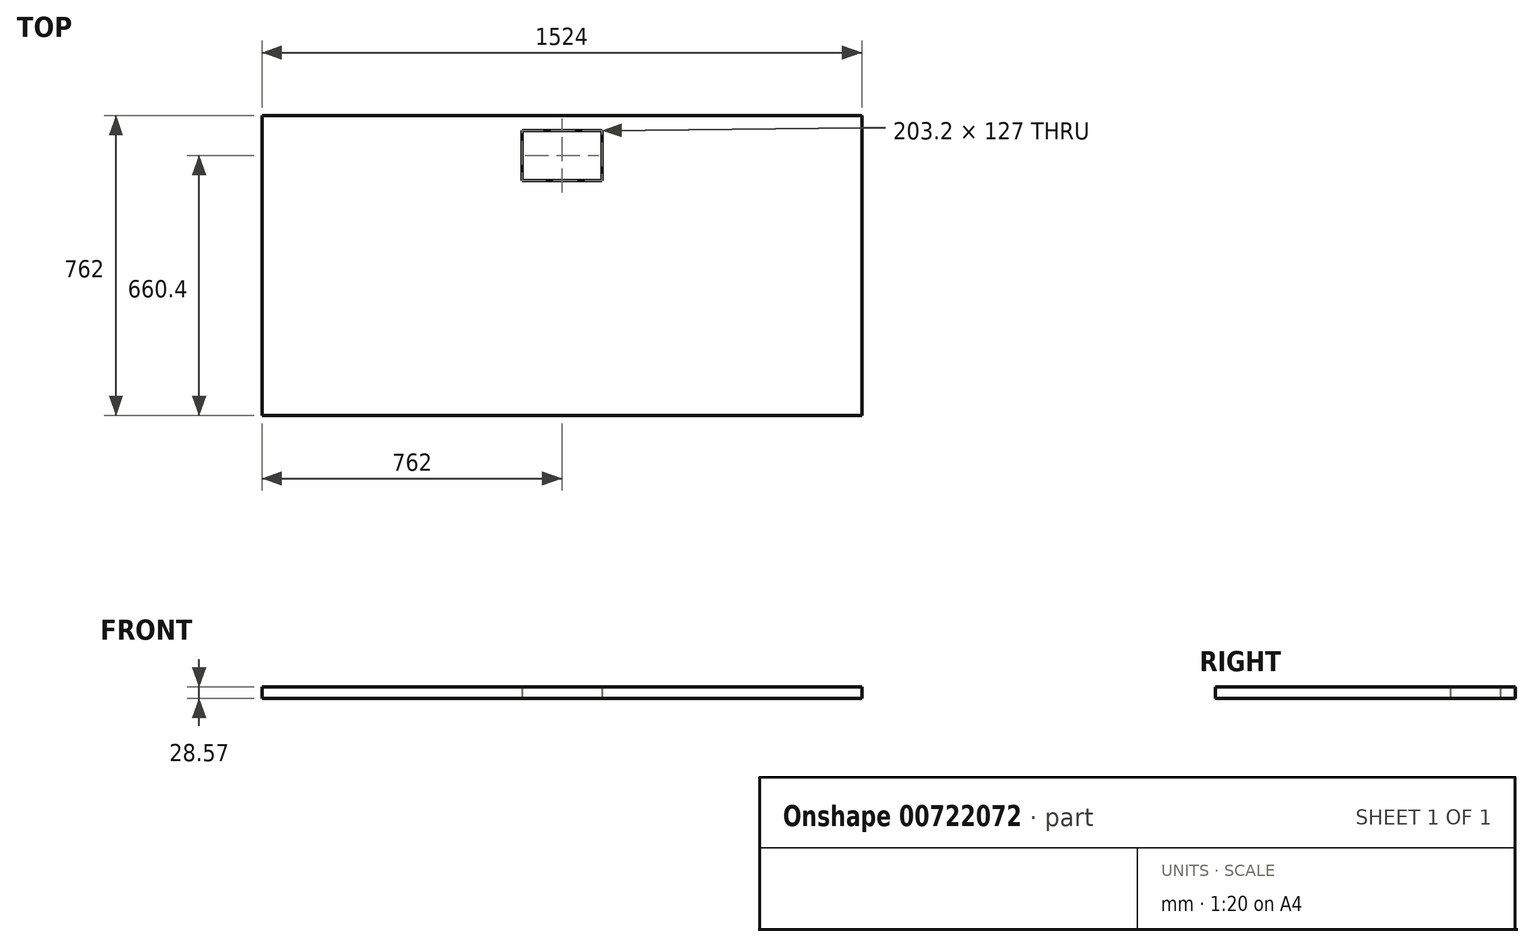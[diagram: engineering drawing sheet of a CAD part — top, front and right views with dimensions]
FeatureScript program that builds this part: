
annotation { "Feature Type Name" : "Feature", "Feature Type Description" : "" }
export const myFeature = defineFeature(function(context is Context, id is Id, definition is map)
    precondition{}
    {
        {
            var Q0;
            Q0=qCreatedBy(makeId("Top.planeOp"),FACE);
            var sketch = newSketch(context, id + "F0", { "sketchPlane" : qUnion([Q0])});
            skLineSegment(sketch, "E0.bottom", {"start": v(762, 381) * mm, "end": v(-762, 381) * mm});
            skLineSegment(sketch, "E0.top", {"start": v(762, -381) * mm, "end": v(-762, -381) * mm});
            skLineSegment(sketch, "E0.left", {"start": v(762, 381) * mm, "end": v(762, -381) * mm});
            skLineSegment(sketch, "E0.right", {"start": v(-762, 381) * mm, "end": v(-762, -381) * mm});
            skPoint(sketch, "E0.middle", {"position": v(0, 0) * mm});
            skLineSegment(sketch, "E1", {"start": v(0, 381) * mm, "end": v(0, 279.4) * mm});
            skLineSegment(sketch, "E2.bottom", {"start": v(-101.6, 342.9) * mm, "end": v(101.6, 342.9) * mm});
            skLineSegment(sketch, "E2.top", {"start": v(-101.6, 215.9) * mm, "end": v(101.6, 215.9) * mm});
            skLineSegment(sketch, "E2.left", {"start": v(-101.6, 342.9) * mm, "end": v(-101.6, 215.9) * mm});
            skLineSegment(sketch, "E2.right", {"start": v(101.6, 342.9) * mm, "end": v(101.6, 215.9) * mm});
            skPoint(sketch, "E2.middle", {"position": v(0, 279.4) * mm});
            skSolve(sketch);
        }
        {
            var Q0;
            Q0=makeQuery(id+"F0.imprint","IMPRINT",FACE,{"disambiguationData":[TD([[makeQuery(id+"F0.imprint","IMPRINT",EDGE,{"derivedFrom":sQuery(id+"F0.wireOp",EDGE,"E0.bottom")}),1.0]])]});
            extrude(context, id + "F1", {"entities" : qUnion([Q0]), "depth" : 28.57 * mm, "offsetDistance" : 25.4 * mm});
        }
    });
